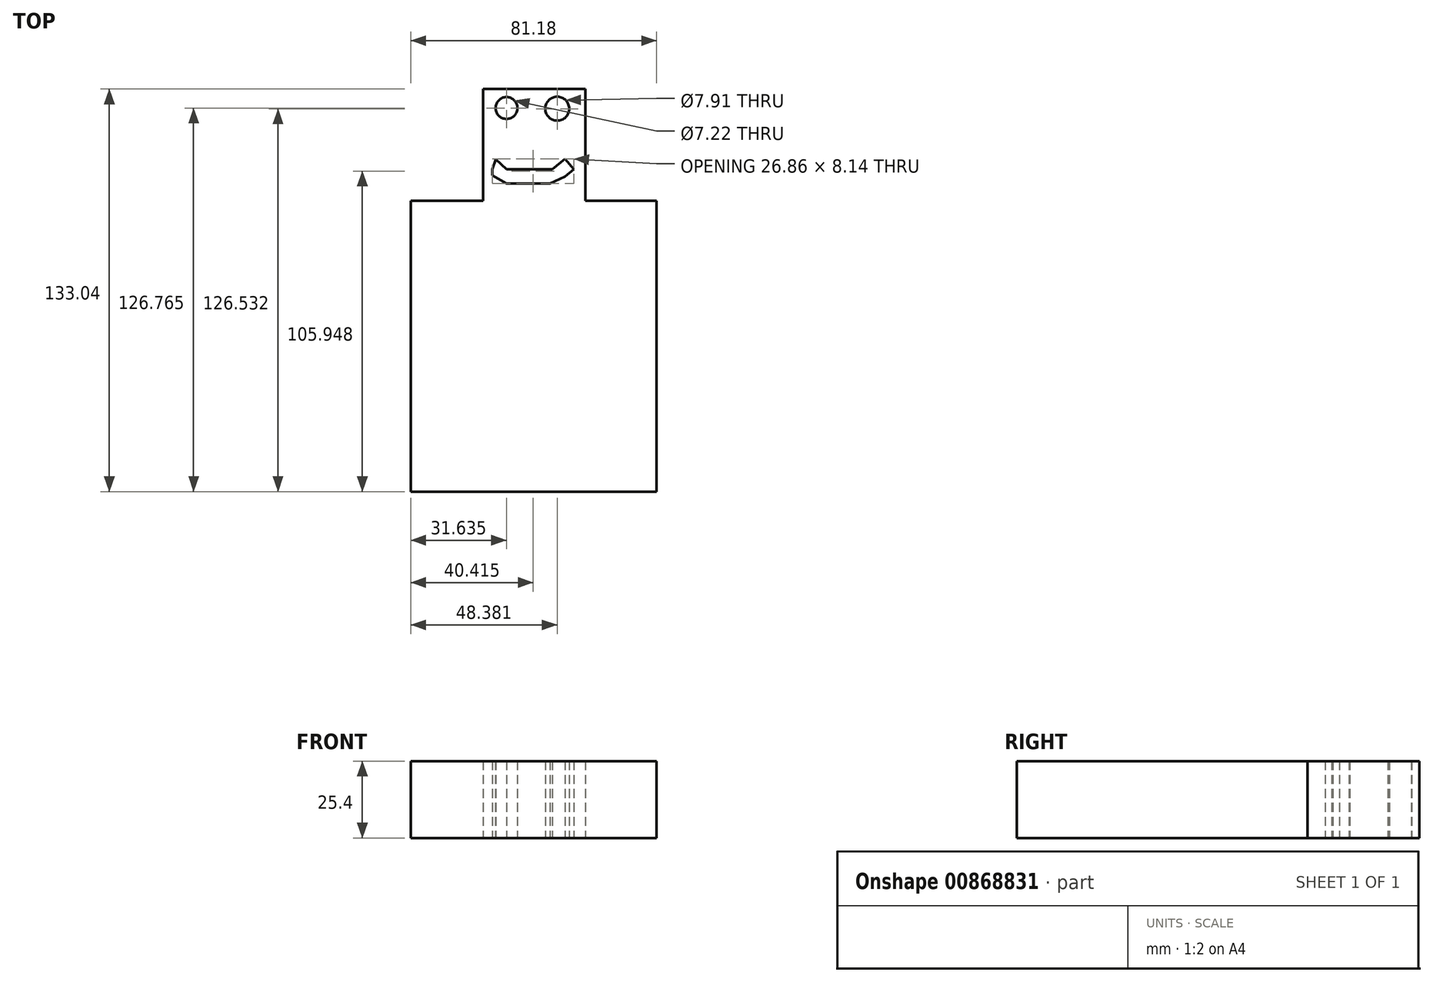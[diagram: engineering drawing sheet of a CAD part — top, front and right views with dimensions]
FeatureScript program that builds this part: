
annotation { "Feature Type Name" : "Feature", "Feature Type Description" : "" }
export const myFeature = defineFeature(function(context is Context, id is Id, definition is map)
    precondition{}
    {
        {
            var Q0;
            Q0=qCreatedBy(makeId("Top.planeOp"),FACE);
            var sketch = newSketch(context, id + "F0", { "sketchPlane" : qUnion([Q0])});
            skLineSegment(sketch, "E0.bottom", {"start": v(-17.56, 75.47) * mm, "end": v(16.16, 75.47) * mm});
            skLineSegment(sketch, "E0.top", {"start": v(-17.56, 38.5) * mm, "end": v(16.16, 38.5) * mm});
            skLineSegment(sketch, "E0.left", {"start": v(-17.56, 75.47) * mm, "end": v(-17.56, 38.5) * mm});
            skLineSegment(sketch, "E0.right", {"start": v(16.16, 75.47) * mm, "end": v(16.16, 38.5) * mm});
            skLineSegment(sketch, "E1.bottom", {"start": v(-41.52, 38.5) * mm, "end": v(39.66, 38.5) * mm});
            skLineSegment(sketch, "E1.top", {"start": v(-41.52, -57.57) * mm, "end": v(39.66, -57.57) * mm});
            skLineSegment(sketch, "E1.left", {"start": v(-41.52, 38.5) * mm, "end": v(-41.52, -57.57) * mm});
            skLineSegment(sketch, "E1.right", {"start": v(39.66, 38.5) * mm, "end": v(39.66, -57.57) * mm});
            skCircle(sketch, "E2", {"center": v(-9.88, 69.2) * mm, "radius": 3.61 * mm});
            skCircle(sketch, "E3", {"center": v(6.86, 68.96) * mm, "radius": 3.95 * mm});
            skLineSegment(sketch, "E4", {"start": v(-13.37, 52.22) * mm, "end": v(-9.88, 48.96) * mm});
            skLineSegment(sketch, "E5", {"start": v(-9.88, 48.96) * mm, "end": v(5.23, 48.96) * mm});
            skLineSegment(sketch, "E6", {"start": v(5.23, 48.96) * mm, "end": v(9.42, 52.45) * mm});
            skLineSegment(sketch, "E7", {"start": v(9.42, 52.45) * mm, "end": v(12.33, 48.96) * mm});
            skLineSegment(sketch, "E8", {"start": v(12.33, 48.96) * mm, "end": v(9.42, 46.54) * mm});
            skLineSegment(sketch, "E9", {"start": v(9.42, 46.54) * mm, "end": v(4.54, 44.3) * mm});
            skLineSegment(sketch, "E10", {"start": v(4.54, 44.3) * mm, "end": v(-9.88, 44.3) * mm});
            skLineSegment(sketch, "E11", {"start": v(-9.88, 44.3) * mm, "end": v(-14.54, 46.87) * mm});
            skLineSegment(sketch, "E12", {"start": v(-14.54, 46.87) * mm, "end": v(-14.54, 48.96) * mm});
            skLineSegment(sketch, "E13", {"start": v(-14.54, 48.96) * mm, "end": v(-13.37, 52.22) * mm});
            skLineSegment(sketch, "E14", {"start": v(-5.7, 61.52) * mm, "end": v(-5.7, 55) * mm});
            skLineSegment(sketch, "E15", {"start": v(-5.7, 55) * mm, "end": v(0, 55) * mm});
            skSolve(sketch);
        }
        {
            var Q0;
            Q0 = qSketchRegion(id + "F0", true);
            extrude(context, id + "F1", {"entities" : qUnion([Q0]), "depth" : 25.4 * mm, "offsetDistance" : 25.4 * mm});
        }
    });
